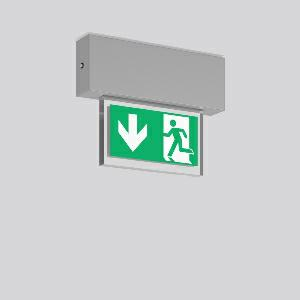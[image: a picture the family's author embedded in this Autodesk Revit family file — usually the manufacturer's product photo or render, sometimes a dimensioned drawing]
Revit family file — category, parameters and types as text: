
# Revit family: halyxx_672458_004_1_04_4dea
name_source: partatom
category: Lighting Fixtures
units: mm (PartAtom-declared; Revit-internal decimal feet)

## family parameters
Cut with Voids When Loaded = No
Host = Face
Light Source = No
Part Type = Normal
Room Calculation Point = No
Round Connector Dimension = Use Diameter
Shared = No

## types (1)
- HALYXX (1 x LED Modul 840, 55 lm, 4000)
    Apparent Load = 3 VA
    Approval mark = CE
    CIE Flux Codes = 18 46 75 53 100
    Color Rendering = 80
    Color Temperature = 4000
    Default Elevation = 1800 mm
    Description = Series: HALYXX
Luminaire for escape route identification. Housing: extruded aluminium profile, anodised or powder-coated. Display panel: highly transparent panel, plastic, with legend on one side/both sides. Electronic ballast included. Self-contained system with automatic self-test and feedback to the RZB monitoring system MULTIDIGIT. Please indicate legend number when placing your order! 
Colour: anodised aluminium
Length: 233 mm
Width: 40 mm
Height: 184 mm
Weight: 1.04 kg
Operating mode: maintained power mode
Viewing Distance: 14 m
Duration time: 8 h
Lamp: LED
Socket: without socket
Colour temperature: 4000K
Colour rendering index (CRI): 80
System power: 3.2 W
Rated luminous flux: 55 lm
Luminous flux, emergency: 10
System power, emergency: -
Control gear: EB
Protection class: I
Type of protection: IP 40
    Height = 184 mm
    Lamp = 1 x LED Modul 840
    Lamp Light Flux = 55 lm
    Lamp count = 1
    Length = 233 mm
    Lifetime = 50000 h
    Luminous efficacy = 17 lm/W
    Manufacturer = RZB
    ModVariant = No
    Model = 672458.004.1.04
    Mounting Place = Ceiling
    Mounting Type = Surface mounted
    Number of Poles = 1
    OnlyDefault = Yes
    Power Factor = 1
    Product Name = HALYXX
    Product group = Surface mounted ceiling luminaires
    ProductGroupID = 303
    Protection Class = Protection class I
    Protection Degree = IP 40
    RLX_Detail_Level = 1
    RLX_Emergency_Light_Flux = 10 lm
    RLX_Emergency_Type = 3
    RLX_Emergency_Type_DB = Yes
    RlxData = <blob elided: 36649 chars, md5=23d2e51b>
    Socket = socket
    Standby Power = 0 W
    System Light Flux = 55 lm
    System Power = 3 W
    Type Comments = Product without accessories
    Type Image = 671502.004.jpg
    URL = http://relux.com
    VarID = ---
    Voltage = 230 V
    Voltage Range = 220-240 V
    Weight = 0.00 kg
    Width = 40 mm  [stored 0.131234 ft]

note: [stored X ft] marks values corroborated as IEEE doubles in the binary element streams (Revit-internal decimal feet)

## geometry (parser evidence)
native form markers: Blend x4, Sweep x11
no freeform markers — native parametric forms only
